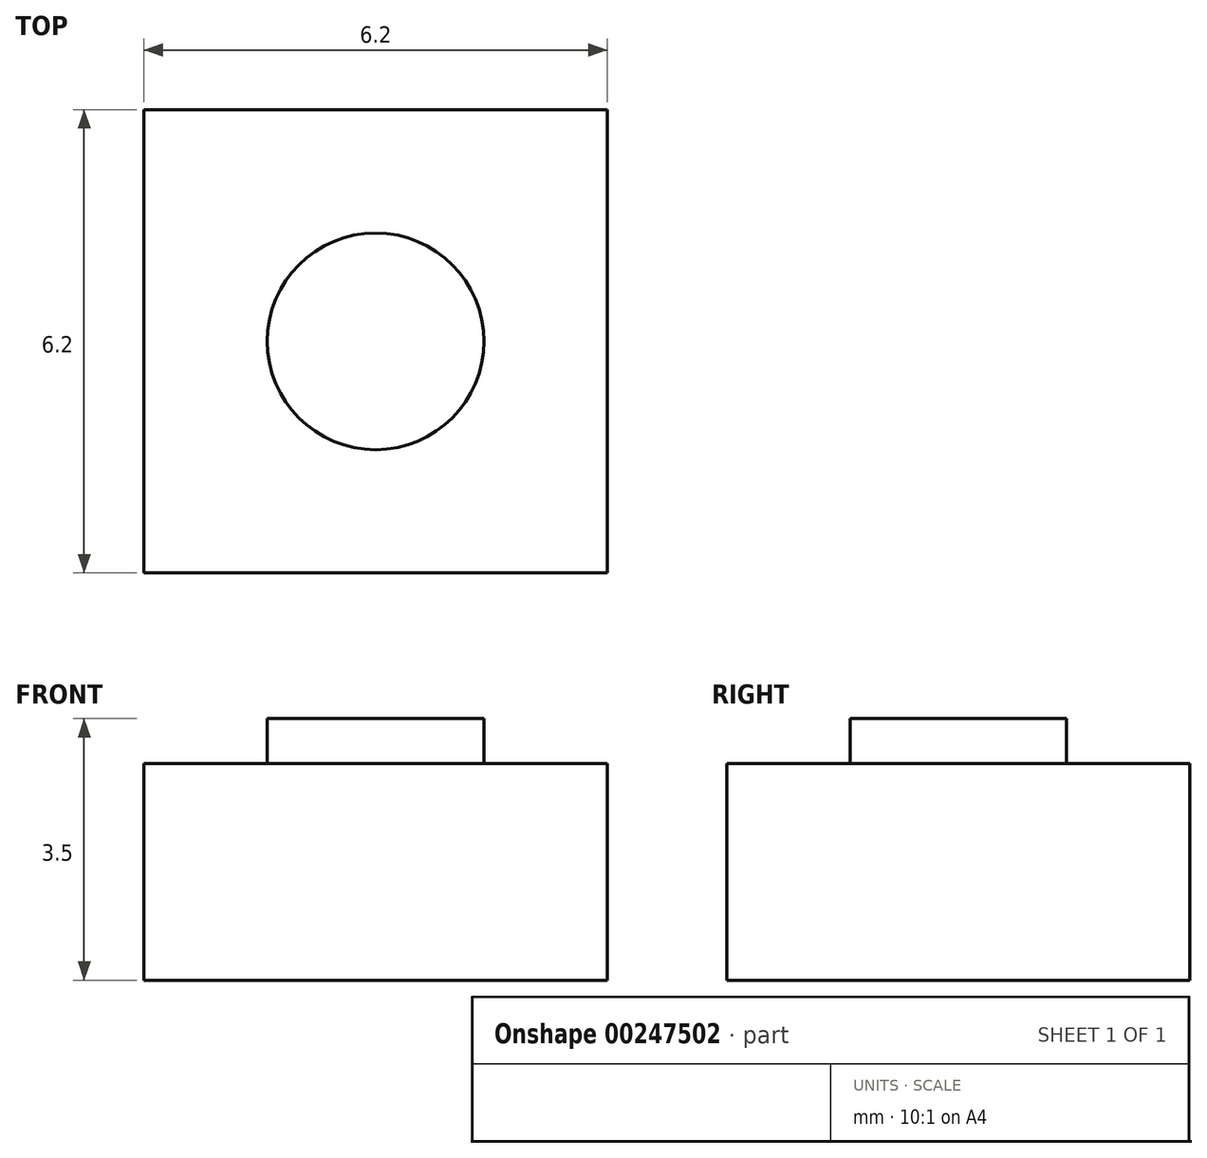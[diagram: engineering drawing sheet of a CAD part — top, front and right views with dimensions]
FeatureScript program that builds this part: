
annotation { "Feature Type Name" : "Feature", "Feature Type Description" : "" }
export const myFeature = defineFeature(function(context is Context, id is Id, definition is map)
    precondition{}
    {
        {
            var Q0;
            Q0=qCreatedBy(makeId("Top.planeOp"),FACE);
            var sketch = newSketch(context, id + "F0", { "sketchPlane" : qUnion([Q0])});
            skLineSegment(sketch, "E0.bottom", {"start": v(3.1, -3.1) * mm, "end": v(-3.1, -3.1) * mm});
            skLineSegment(sketch, "E0.top", {"start": v(3.1, 3.1) * mm, "end": v(-3.1, 3.1) * mm});
            skLineSegment(sketch, "E0.left", {"start": v(3.1, -3.1) * mm, "end": v(3.1, 3.1) * mm});
            skLineSegment(sketch, "E0.right", {"start": v(-3.1, -3.1) * mm, "end": v(-3.1, 3.1) * mm});
            skPoint(sketch, "E0.middle", {"position": v(0, 0) * mm});
            skSolve(sketch);
        }
        {
            var Q0;
            Q0=qSketchRegion(id+"F0",true);
            extrude(context, id + "F1", {"entities" : qUnion([Q0]), "depth" : 2.9 * mm});
        }
        {
            var Q0;
            Q0=makeQuery(id+"F1.opExtrude","CAP_FACE",FACE,{"disambiguationData":[OSD([sQuery(id+"F0.wireOp",EDGE,"E0.bottom"),sQuery(id+"F0.wireOp",EDGE,"E0.top"),sQuery(id+"F0.wireOp",EDGE,"E0.left"),sQuery(id+"F0.wireOp",EDGE,"E0.right")])],"isStart":false});
            var sketch = newSketch(context, id + "F2", { "sketchPlane" : qUnion([Q0])});
            skCircle(sketch, "E1", {"center": v(0, 0) * mm, "radius": 1.45 * mm});
            skSolve(sketch);
        }
        {
            var Q0;
            Q0=qSketchRegion(id+"F2",true);
            extrude(context, id + "F3", {"entities" : qUnion([Q0]), "depth" : .6 * mm});
        }
    });
